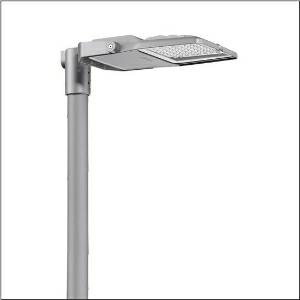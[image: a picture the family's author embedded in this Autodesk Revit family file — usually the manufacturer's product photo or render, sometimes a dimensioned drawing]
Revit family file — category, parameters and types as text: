
# Revit family: floodlight_fl_21_iq_mini___pl52_5xa7772c4d3a_40ba
name_source: partatom
category: Lighting Fixtures
units: mm (PartAtom-declared; Revit-internal decimal feet)

## family parameters
Cut with Voids When Loaded = No
Host = Face
Light Source = No
Part Type = Normal
Room Calculation Point = No
Round Connector Dimension = Use Diameter
Shared = No

## types (1)
- --- (1 x LED, 12720 lm, 87.2 W, 4000K)
    Apparent Load = 87 VA
    CIE Flux Codes = 26 60 98 100 100
    Color Rendering = 70
    Color Temperature = 4000K
    Default Elevation = 1800 mm
    Description = Floodlight FL 21 iQ mini, floodlight, primary light control with lens, of PMMA, primary optical cover: protective disc, of toughened safety glass, transparent, light distribution: PL52, light emission: direct distribution, installation type: surface-mounted, LED, High Power LED, rated luminous flux: 12.720lm, luminous efficacy: 146lm/W, light colour: 740, colour temperature: 4000K, control gear: iQ Street-Remote/DALI, control: Auto-Match, Temp-Guard, Night-Set, Smart-Wire, Desk-Remote (wireless, voltage-free reading and setting of iQ features in the workshop via application-optimized NFC function/RFID function), optimised constant luminous flux control (CLO 2.0), Light-Fading, Lumen-Switch, with terminal, 6-pole, mains connection: 220..240V, AC, 50/60Hz, start of lifetime: 87W, end of service life: 92W, reduction: 40W, luminaire housing, of diecast aluminium, powder-coated, Siteco® metallic grey (DB 702S), corrosivity category C5 mid according to DIN EN ISO 12944, suitable for swimming pools, chlorine-resistant, sealing non-destructively replaceable, please order mast flange separately, mast bracket, of steel, galvanised, powder-coated, protection rating (complete): IP66, insulation class (complete): insulation class II (safety insulation), certification: CE, ENEC, VDE, protection symbol: D, impact resistance: IK08, permissible operating ambient temperature: -40..+40°C, permissible operating ambient temperature for outdoor applications: -40..+50°C, standard: DIN EN 12944, LABS conformity tested according to VDMA 24364:2018-05, packaging unit: 1 piece

Light Distribution: PL52
    Height = 70 mm
    Lamp = 1 x LED
    Lamp Light Flux = 12720 lm
    Lamp Power = 87.2 W
    Lamp count = 1
    Length = 485 mm
    Luminous efficacy = 146 lm/W
    Manufacturer = Siteco
    ModVariant = No
    Model = 5XA7772C4D3A
    Number of Poles = 1
    OnlyDefault = Yes
    Power Factor = 1
    Product Name = Floodlight FL 21 iQ mini | PL52
    Product group = floodlight | pylon annexe
    ProductGroupID = 6201
    Protection Class = Protection class II
    Protection Degree = IP 66
    RLX_Detail_Level = 1
    RLX_Emergency_Light_Flux = 0 lm
    RLX_Emergency_Type = 0
    RLX_Emergency_Type_DB = No
    RlxData = <blob elided: 101657 chars, md5=52456d17>
    Socket = socket
    Standby Power = 0 W
    System Light Flux = 12720 lm
    System Power = 87 W
    Type Comments = factory setting: luminous flux: 100 % | dim-lin: 254 | 456 mA
    Type Image = l_1007125.jpg
    URL = http://relux.com
    VarID = @adj_185617
    Voltage = 0 V
    Weight = 0.00 kg
    Width = 337 mm

## geometry (parser evidence)
native form markers: Blend x4, Sweep x13
no freeform markers — native parametric forms only
